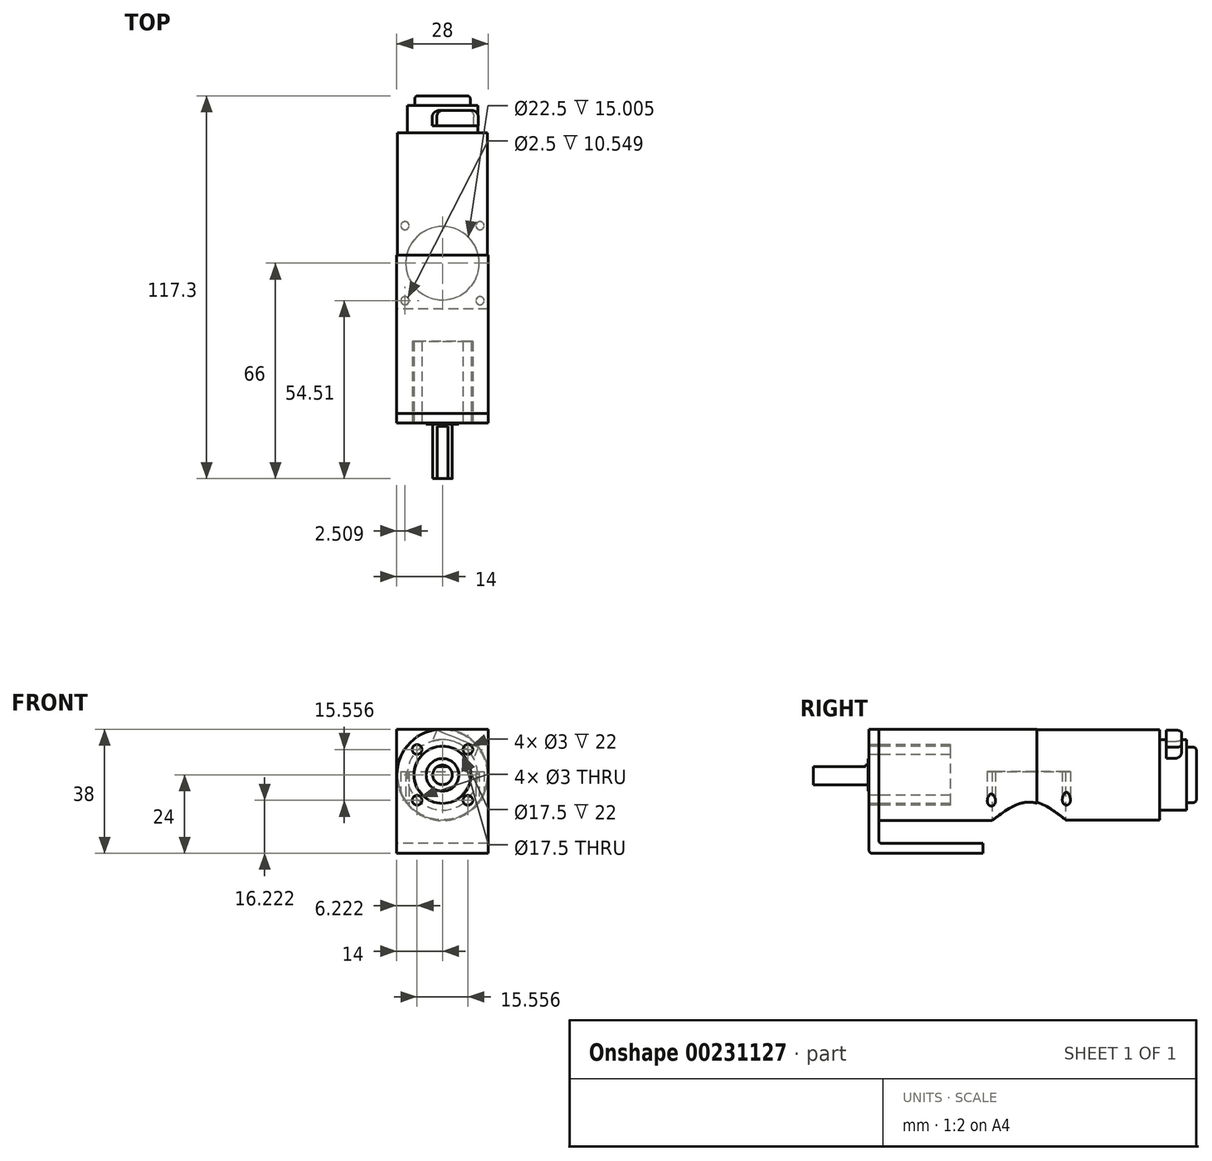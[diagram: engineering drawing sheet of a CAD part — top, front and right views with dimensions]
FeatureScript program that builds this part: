
annotation { "Feature Type Name" : "Feature", "Feature Type Description" : "" }
export const myFeature = defineFeature(function(context is Context, id is Id, definition is map)
    precondition{}
    {
        {
            var Q0;
            Q0=qCreatedBy(makeId("Right.planeOp"),FACE);
            var sketch = newSketch(context, id + "F0", { "sketchPlane" : qUnion([Q0])});
            skLineSegment(sketch, "E0", {"start": v(0, 0) * mm, "end": v(-20, 0) * mm});
            skLineSegment(sketch, "E1", {"start": v(-20, 0) * mm, "end": v(-20, 3) * mm});
            skLineSegment(sketch, "E2", {"start": v(-20, 3) * mm, "end": v(-3.3, 3) * mm});
            skLineSegment(sketch, "E3", {"start": v(-3.3, 3) * mm, "end": v(-3.3, 5) * mm});
            skLineSegment(sketch, "E4", {"start": v(-3.3, 5) * mm, "end": v(-2, 5) * mm});
            skLineSegment(sketch, "E5", {"start": v(-2, 5) * mm, "end": v(-2, 8.5) * mm});
            skLineSegment(sketch, "E6", {"start": v(-2, 8.5) * mm, "end": v(0, 8.5) * mm});
            skLineSegment(sketch, "E7", {"start": v(0, 8.5) * mm, "end": v(0, 14) * mm});
            skLineSegment(sketch, "E8", {"start": v(0, 14) * mm, "end": v(48.5, 14) * mm});
            skLineSegment(sketch, "E9", {"start": v(48.5, 14) * mm, "end": v(48.5, 13.8) * mm});
            skLineSegment(sketch, "E10", {"start": v(48.5, 13.8) * mm, "end": v(86, 13.8) * mm});
            skLineSegment(sketch, "E11", {"start": v(86, 13.8) * mm, "end": v(86, 10.8) * mm});
            skLineSegment(sketch, "E12", {"start": v(86, 10.8) * mm, "end": v(94.3, 10.8) * mm});
            skLineSegment(sketch, "E13", {"start": v(94.3, 10.8) * mm, "end": v(94.3, 8.5) * mm});
            skLineSegment(sketch, "E14", {"start": v(94.3, 8.5) * mm, "end": v(97.3, 8.5) * mm});
            skLineSegment(sketch, "E15", {"start": v(97.3, 8.5) * mm, "end": v(97.3, 0) * mm});
            skLineSegment(sketch, "E16", {"start": v(97.3, 0) * mm, "end": v(0, 0) * mm});
            skSolve(sketch);
        }
        {
            var Q0;
            Q0=makeQuery(id+"F0.imprint","IMPRINT",FACE,{"disambiguationData":[TD([[makeQuery(id+"F0.imprint","IMPRINT",EDGE,{"derivedFrom":sQuery(id+"F0.wireOp",EDGE,"E0")}),-1.0]])]});
            var Q1;
            Q1=sQuery(id+"F0.wireOp",EDGE,"E16");
            revolve(context, id + "F1", {"entities" : qUnion([Q0]), "axis" : qUnion([Q1]), "revolveType" : RevolveType.FULL});
        }
        {
            var Q0;
            Q0=makeQuery(id+"F1.opRevolve","SWEPT_FACE",FACE,{"disambiguationData":[OSD([sQuery(id+"F0.wireOp",EDGE,"E1")])]});
            var sketch = newSketch(context, id + "F2", { "sketchPlane" : qUnion([Q0])});
            skArc(sketch, "E17.0", {"start": v(1.66, 2.5) * mm, "mid": v(0, 3) * mm, "end": v(-1.66, 2.5) * mm});
            skLineSegment(sketch, "E18", {"start": v(-1.66, 2.5) * mm, "end": v(1.66, 2.5) * mm});
            skSolve(sketch);
        }
        {
            var Q0;
            Q0=makeQuery(id+"F2.imprint","IMPRINT",FACE,{"disambiguationData":[TD([[makeQuery(id+"F2.imprint","IMPRINT",EDGE,{"derivedFrom":sQuery(id+"F2.wireOp",EDGE,"E17.0")}),-1.0]])]});
            extrude(context, id + "F3", {"entities" : qUnion([Q0]), "operationType" : NewBodyOperationType.REMOVE, "oppositeDirection" : true, "depth" : 16 * mm});
        }
        {
            var Q0;
            Q0=makeQuery(id+"F1.opRevolve","SWEPT_FACE",FACE,{"disambiguationData":[OSD([sQuery(id+"F0.wireOp",EDGE,"E7")])]});
            var sketch = newSketch(context, id + "F4", { "sketchPlane" : qUnion([Q0])});
            skCircle(sketch, "E19", {"center": v(7.78, 7.78) * mm, "radius": 1.5 * mm});
            skCircle(sketch, "E20.1.0", {"center": v(-7.78, 7.78) * mm, "radius": 1.5 * mm});
            skCircle(sketch, "E20.2.0", {"center": v(-7.78, -7.78) * mm, "radius": 1.5 * mm});
            skCircle(sketch, "E20.3.0", {"center": v(7.78, -7.78) * mm, "radius": 1.5 * mm});
            skPoint(sketch, "E20.center", {"position": v(0, 0) * mm});
            skSolve(sketch);
        }
        {
            var Q0;
            Q0=makeQuery(id+"F4.imprint","IMPRINT",FACE,{"disambiguationData":[TD([[makeQuery(id+"F4.imprint","IMPRINT",EDGE,{"derivedFrom":sQuery(id+"F4.wireOp",EDGE,"E19")}),1.0]])]});
            extrude(context, id + "F5", {"entities" : qUnion([Q0]), "operationType" : NewBodyOperationType.REMOVE, "oppositeDirection" : true, "depth" : 3.5 * mm});
        }
        {
            var Q0;
            Q0=makeQuery(id+"F1.opRevolve","SWEPT_EDGE",EDGE,{"disambiguationData":[OSD([sQuery(id+"F0.wireOp",EDGE,"E14"),sQuery(id+"F0.wireOp",EDGE,"E15")])]});
            fillet(context, id + "F6", {"entities" : qUnion([Q0]), "radius" : 1 * mm, "tangentPropagation" : true, "allowEdgeOverflow" : false});
        }
        {
            var Q0;
            Q0=sQuery(id+"F0.wireOp",EDGE,"E16");
            cPlane(context, id + "F7", {"entities" : qUnion([Q0]), "cplaneType" : CPlaneType.LINE_ANGLE, "offset" : 25 * mm, "angle" : 157.5 * degree, "width" : 150 * mm, "height" : 150 * mm});
        }
        {
            var Q0;
            Q0=qCreatedBy(id+"F7.planeOp",FACE);
            var sketch = newSketch(context, id + "F8", { "sketchPlane" : qUnion([Q0])});
            skLineSegment(sketch, "E21.bottom", {"start": v(6.9, 92.79) * mm, "end": v(-6.9, 92.79) * mm});
            skLineSegment(sketch, "E21.top", {"start": v(6.9, 88.09) * mm, "end": v(-6.9, 88.09) * mm});
            skLineSegment(sketch, "E21.left", {"start": v(6.9, 92.79) * mm, "end": v(6.9, 88.09) * mm});
            skLineSegment(sketch, "E21.right", {"start": v(-6.9, 92.79) * mm, "end": v(-6.9, 88.09) * mm});
            skPoint(sketch, "E21.middle", {"position": v(0, 90.44) * mm});
            skSolve(sketch);
        }
        {
            var Q0;
            Q0 = qSketchRegion(id + "F8", true);
            extrude(context, id + "F9", {"entities" : qUnion([Q0]), "operationType" : NewBodyOperationType.ADD, "depth" : 12 * mm});
        }
        {
            var Q0;
            Q0=makeQuery(id+"F9.opExtrude","SWEPT_EDGE",EDGE,{"disambiguationData":[OSD([sQuery(id+"F8.wireOp",EDGE,"E21.bottom"),sQuery(id+"F8.wireOp",EDGE,"E21.left")])]});
            var Q1;
            Q1=makeQuery(id+"F9.opExtrude","SWEPT_EDGE",EDGE,{"disambiguationData":[OSD([sQuery(id+"F8.wireOp",EDGE,"E21.bottom"),sQuery(id+"F8.wireOp",EDGE,"E21.right")])]});
            fillet(context, id + "F10", {"entities" : qUnion([Q0, Q1]), "radius" : 2 * mm, "tangentPropagation" : true, "allowEdgeOverflow" : false});
        }
        {
            var Q0;
            Q0=qCreatedBy(makeId("Right.planeOp"),FACE);
            var sketch = newSketch(context, id + "F11", { "sketchPlane" : qUnion([Q0])});
            skLineSegment(sketch, "E22.0", {"start": v(0, -21) * mm, "end": v(0, 14) * mm});
            skLineSegment(sketch, "E23.0", {"start": v(0, 0) * mm, "end": v(-20, 0) * mm, "construction": true});
            skLineSegment(sketch, "E24", {"start": v(0, 14) * mm, "end": v(-19.97, 14) * mm, "construction": true});
            skPoint(sketch, "E25.orphan", {"position": v(0, 14) * mm});
            skPoint(sketch, "E26.orphan", {"position": v(0, 8.5) * mm});
            skLineSegment(sketch, "E27", {"start": v(0, 14) * mm, "end": v(-3, 14) * mm});
            skLineSegment(sketch, "E28", {"start": v(-3, 14) * mm, "end": v(-3, -24) * mm});
            skLineSegment(sketch, "E29", {"start": v(-3, -24) * mm, "end": v(32, -24) * mm});
            skLineSegment(sketch, "E30", {"start": v(32, -24) * mm, "end": v(32, -21) * mm});
            skLineSegment(sketch, "E31", {"start": v(32, -21) * mm, "end": v(0, -21) * mm});
            skSolve(sketch);
        }
        {
            var Q0;
            Q0=makeQuery(id+"F11.imprint","IMPRINT",FACE,{"disambiguationData":[TD([[makeQuery(id+"F11.imprint","IMPRINT",EDGE,{"derivedFrom":sQuery(id+"F11.wireOp",EDGE,"E22.0")}),1.0]])]});
            extrude(context, id + "F12", {"entities" : qUnion([Q0]), "endBound" : BoundingType.SYMMETRIC, "depth" : 28 * mm, "hasSecondDirection" : true, "secondDirectionOppositeDirection" : true, "secondDirectionDepth" : 25 * mm});
        }
        {
            var Q0;
            Q0=makeQuery(id+"F12.opExtrude","SWEPT_EDGE",EDGE,{"disambiguationData":[OSD([sQuery(id+"F11.wireOp",EDGE,"E22.0"),sQuery(id+"F11.wireOp",EDGE,"E31")])]});
            var Q1;
            Q1=makeQuery(id+"F12.opExtrude","SWEPT_EDGE",EDGE,{"disambiguationData":[OSD([sQuery(id+"F11.wireOp",EDGE,"E28"),sQuery(id+"F11.wireOp",EDGE,"E29")])]});
            fillet(context, id + "F13", {"entities" : qUnion([Q0, Q1]), "radius" : 1 * mm, "tangentPropagation" : true, "allowEdgeOverflow" : false});
        }
        {
            var Q0;
            Q0=makeQuery(id+"F12.opExtrude","SWEPT_FACE",FACE,{"disambiguationData":[OSD([sQuery(id+"F11.wireOp",EDGE,"E28")])]});
            var sketch = newSketch(context, id + "F14", { "sketchPlane" : qUnion([Q0])});
            skPoint(sketch, "E32.0", {"position": v(0, 0) * mm});
            skCircle(sketch, "E33", {"center": v(0, 0) * mm, "radius": 8.75 * mm});
            skCircle(sketch, "E34", {"center": v(-7.78, 7.78) * mm, "radius": 1.5 * mm});
            skCircle(sketch, "E35.1.0", {"center": v(-7.78, -7.78) * mm, "radius": 1.5 * mm});
            skCircle(sketch, "E35.2.0", {"center": v(7.78, -7.78) * mm, "radius": 1.5 * mm});
            skCircle(sketch, "E35.3.0", {"center": v(7.78, 7.78) * mm, "radius": 1.5 * mm});
            skSolve(sketch);
        }
        {
            var Q0;
            Q0 = qSketchRegion(id + "F14", true);
            extrude(context, id + "F15", {"entities" : qUnion([Q0]), "operationType" : NewBodyOperationType.REMOVE, "oppositeDirection" : true, "depth" : 25 * mm});
        }
        {
            var Q0;
            Q0=makeQuery(id+"F12.opExtrude","SWEPT_FACE",FACE,{"disambiguationData":[OSD([sQuery(id+"F11.wireOp",EDGE,"E29")])]});
            var sketch = newSketch(context, id + "F16", { "sketchPlane" : qUnion([Q0])});
            skLineSegment(sketch, "E36", {"start": v(0, -32) * mm, "end": v(0, -46) * mm, "construction": true});
            skCircle(sketch, "E37", {"center": v(0, -46) * mm, "radius": 11.25 * mm});
            skLineSegment(sketch, "E38", {"start": v(0, -46) * mm, "end": v(-11.5, -34.5) * mm, "construction": true});
            skCircle(sketch, "E39", {"center": v(-11.5, -34.5) * mm, "radius": 1.25 * mm});
            skCircle(sketch, "E40.1.0", {"center": v(-11.5, -57.5) * mm, "radius": 1.25 * mm});
            skCircle(sketch, "E40.2.0", {"center": v(11.5, -57.5) * mm, "radius": 1.25 * mm});
            skCircle(sketch, "E40.3.0", {"center": v(11.5, -34.5) * mm, "radius": 1.25 * mm});
            skSolve(sketch);
        }
        {
            var Q0;
            Q0 = qSketchRegion(id + "F16", true);
            extrude(context, id + "F17", {"entities" : qUnion([Q0]), "operationType" : NewBodyOperationType.REMOVE, "oppositeDirection" : true, "depth" : 25 * mm});
        }
    });
